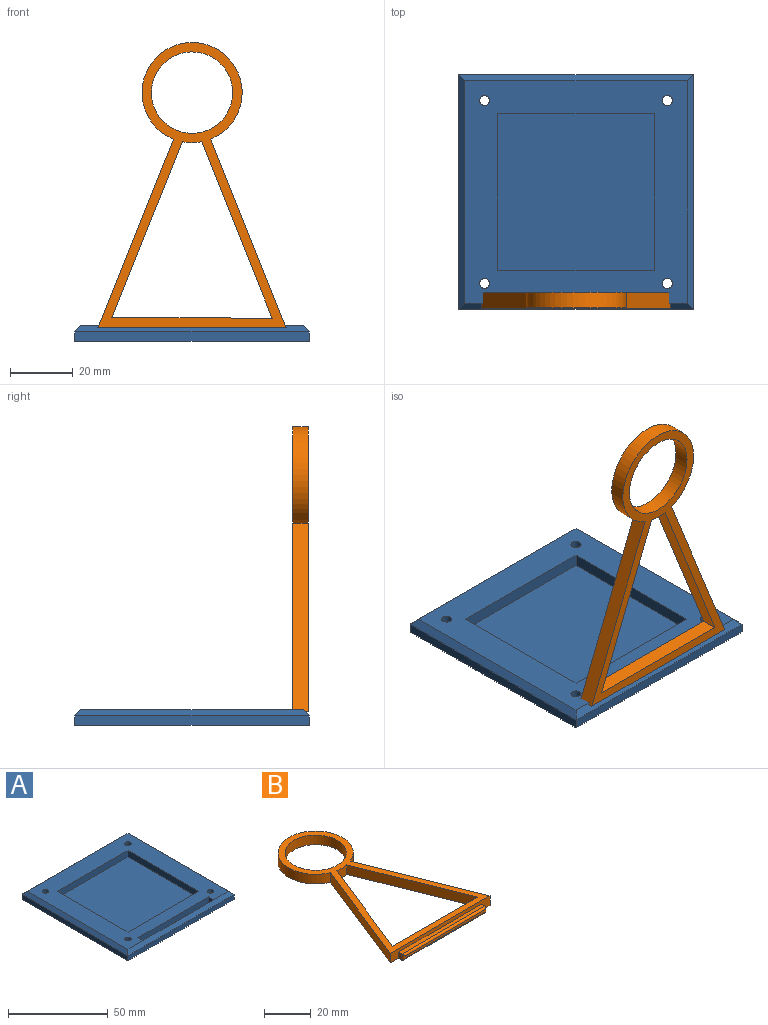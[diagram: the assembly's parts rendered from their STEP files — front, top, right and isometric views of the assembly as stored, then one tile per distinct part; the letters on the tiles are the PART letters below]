
ASSEMBLY  parts=2 mates=1
PART A: 24 faces, bbox 75x75x5 mm
  f0: plane 71x71mm, normal (0,0,1), area 2333.8mm2, adj f4,f5,f6,f7,f10,f11,f12,f13
  f1: plane 75x3mm, normal (0,1,0), area 225mm2, adj f2,f8,f9,f13
  f2: plane 75x3mm, normal (-1,0,0), area 225mm2, adj f1,f3,f9,f11
  f3: plane 75x3mm, normal (0,-1,0), area 225mm2, adj f2,f8,f9,f10
  f4: cylinder r=1.6mm len=5mm, axis (0,0,-1), area 50.3mm2, adj f0,f9
  f5: cylinder r=1.6mm len=5mm, axis (0,0,-1), area 50.3mm2, adj f0,f9
  f6: cylinder r=1.6mm len=5mm, axis (0,0,-1), area 50.3mm2, adj f0,f9
  f7: cylinder r=1.6mm len=5mm, axis (0,0,-1), area 50.3mm2, adj f0,f9
  f8: plane 75x3mm, normal (1,0,0), area 225mm2, adj f1,f3,f9,f12
  f9: plane 75x75mm, normal (0,0,-1), area 5592.8mm2, adj f1,f2,f3,f4,f5,f6,f7,f8
  f10: plane 75x2mm, normal (0,-0.71,0.71), area 206.5mm2, adj f0,f3,f11,f12,f15
  f11: plane 75x2mm, normal (-0.71,0,0.71), area 206.5mm2, adj f0,f2,f10,f13
  f12: plane 75x2mm, normal (0.71,0,0.71), area 206.5mm2, adj f0,f8,f10,f13
  f13: plane 75x2mm, normal (0,0.71,0.71), area 206.5mm2, adj f0,f1,f11,f12
  f14: plane 3.5x3.5mm, normal (1,0,0), area 12.2mm2, adj f0,f15,f17,f18
  f15: plane 50x3.5mm, normal (0,1,0), area 175mm2, adj f10,f14,f16,f18
  f16: plane 3.5x3.5mm, normal (-1,0,0), area 12.2mm2, adj f0,f15,f17,f18
  f17: plane 50x3.5mm, normal (0,-1,0), area 175mm2, adj f0,f14,f16,f18
  f18: plane 50x3.5mm, normal (0,0,1), area 175mm2, adj f14,f15,f16,f17
  f19: plane 50x4mm, normal (0,-1,0), area 200mm2, adj f0,f20,f22,f23
  f20: plane 50x4mm, normal (1,0,0), area 200mm2, adj f0,f19,f21,f23
  f21: plane 50x4mm, normal (0,1,0), area 200mm2, adj f0,f20,f22,f23
  f22: plane 50x4mm, normal (-1,0,0), area 200mm2, adj f0,f19,f21,f23
  f23: plane 50x50mm, normal (0,0,1), area 2500mm2, adj f19,f20,f21,f22
PART B: 19 faces, bbox 60.1x94x5 mm
  f0: cylinder r=16mm len=32mm, axis (0,0,-1), area 441.7mm2, adj f1,f8,f9,f10
  f1: plane 60.14x24.06mm, normal (-0.93,0.37,0), area 323.9mm2, adj f0,f2,f9,f10
  f2: plane 60.07x5mm, normal (0,-1,0), area 140.3mm2, adj f1,f8,f9,f10,f11,f12,f13
  f3: plane 56.29x22.52mm, normal (0.93,-0.37,0), area 303.2mm2, adj f4,f7,f9,f10
  f4: cylinder r=16mm len=6.12mm, axis (0,0,-1), area 30.8mm2, adj f3,f5,f9,f10
  f5: plane 56.3x22.58mm, normal (-0.93,-0.37,0), area 303.3mm2, adj f4,f7,f9,f10
  f6: cylinder r=13mm len=26mm, axis (0,0,-1), area 408.4mm2, adj f9,f10
  f7: plane 51.22x5mm, normal (0,1,0), area 256.1mm2, adj f3,f5,f9,f10
  f8: plane 60.11x24.11mm, normal (0.93,0.37,0), area 323.8mm2, adj f0,f2,f9,f10
  f9: plane 91x60.07mm, normal (0,0,1), area 815mm2, adj f0,f1,f2,f3,f4,f5,f6,f7
  f10: plane 93x60.07mm, normal (0,0,-1), area 915mm2, adj f0,f1,f2,f3,f4,f5,f6,f7
  f11: plane 3.2x2mm, normal (-1,0,0), area 6.4mm2, adj f2,f10,f13,f15
  f12: plane 3.2x2mm, normal (1,0,0), area 6.4mm2, adj f2,f10,f13,f18
  f13: plane 50x2.03mm, normal (0,0,1), area 100mm2, adj f2,f11,f12,f17
  f14: plane 48x1.2mm, normal (0,-1,0), area 57.6mm2, adj f15,f16,f17,f18
  f15: cylinder r=1mm len=3.2mm, axis (0,0,1), area 3.9mm2, adj f11,f14,f16,f17
  f16: cylinder r=1mm len=50mm, axis (-1,0,0), area 77.4mm2, adj f10,f14,f15,f18
  f17: cylinder r=1mm len=50mm, axis (1,0,0), area 77.4mm2, adj f13,f14,f15,f18
  f18: cylinder r=1mm len=3.2mm, axis (0,0,-1), area 3.9mm2, adj f12,f14,f16,f17
PLACE A t=(-6.87,2.81,-19.09)mm fixed
PLACE B rot(axis=(1,0,0),90deg) t=(-99.72,-45.61,22.25)mm
MATE fastened B.f14 <-> A.f18  axis (0,0,-1) through (-4.15,-47.21,-17.59)mm
